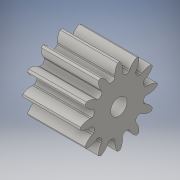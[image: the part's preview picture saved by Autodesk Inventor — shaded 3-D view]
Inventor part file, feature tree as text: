
AUTODESK INVENTOR PART (.ipt)
format: ipt  version: 2016 (Build 200138000, 138)  size: 275,968 bytes
history: native  units: in
note: dims shown in document units (in); Inventor stores cm internally (conversion verified against a paired STEP export)
features: extrude x3, sketch x3, plane x1
ambient origin geometry x8: Origin, YZ Plane, XZ Plane, XY Plane, X Axis, Y Axis, Z Axis, Center Point
bodies: Solid1 (feature_tree)
feature tree (7):
  plane  "Work Plane2"
  extrude  "Extrusion19"  Depth=0.451in TaperAngle=0.0deg
  extrude  "Extrusion20"  Depth=100.0in TaperAngle=0.0deg
  extrude  "Extrusion21"  Depth=4.7244in TaperAngle=360.0deg
  sketch  "Sketch6"  dims[d92=4.7244in d94=360.0deg d102=0.451in d103=0.0in]
  sketch  "Sketch7"  dims[d104=0.128in d105=100.0in d106=0.0in]
  sketch  "Sketch8"  dims[d107=0.4in d108=4.7244in d110=360.0deg d112=100.0in d113=0.0in]
